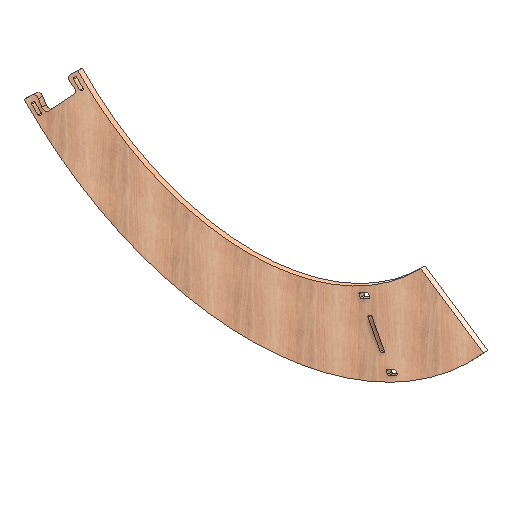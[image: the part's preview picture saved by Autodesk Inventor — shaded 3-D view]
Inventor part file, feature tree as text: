
AUTODESK INVENTOR PART (.ipt)
format: ipt  version: 2021 (Build 250183000, 183)  size: 292,352 bytes
history: native  units: mm
features: other x2, extrude x2, hole x1
ambient origin geometry x8: Origin, YZ Plane, XZ Plane, XY Plane, X Axis, Y Axis, Z Axis, Center Point
bodies: Body1 (feature_tree)
feature tree (5):
  other  "CONTOURS"
  hole  "HOLES"  [1 undecoded]
  other  "LETTERS"
  extrude  "Extrusion4"  Depth=18.0mm TaperAngle=0.0deg
  extrude  "Extrusion5"  [1 undecoded]
note: 2 required parameter values undecoded (feature->parameter linkage not recoverable at this tier; creation-order binding heuristic only, values carry confidence <= 0.55)
